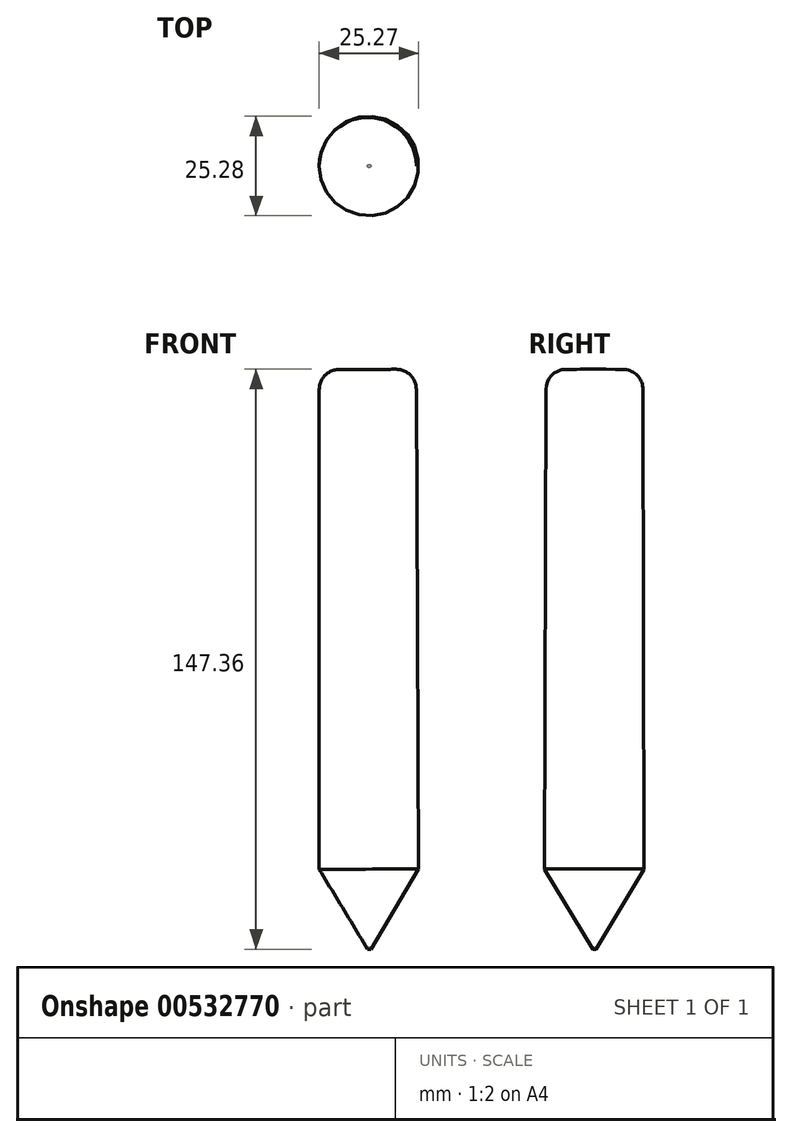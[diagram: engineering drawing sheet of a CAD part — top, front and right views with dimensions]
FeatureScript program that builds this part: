
annotation { "Feature Type Name" : "Feature", "Feature Type Description" : "" }
export const myFeature = defineFeature(function(context is Context, id is Id, definition is map)
    precondition{}
    {
        {
            var Q0;
            Q0=qCreatedBy(makeId("Front.planeOp"),FACE);
            var sketch = newSketch(context, id + "F0", { "sketchPlane" : qUnion([Q0])});
            skLineSegment(sketch, "E0", {"start": v(-60.12, 72.11) * mm, "end": v(-60.12, -54.89) * mm});
            skLineSegment(sketch, "E1", {"start": v(-60.12, 72.11) * mm, "end": v(-34.72, 72.11) * mm});
            skLineSegment(sketch, "E2", {"start": v(-34.72, 72.11) * mm, "end": v(-34.72, -54.89) * mm});
            skLineSegment(sketch, "E3", {"start": v(-60.12, -54.89) * mm, "end": v(-34.72, -54.89) * mm});
            skLineSegment(sketch, "E4", {"start": v(-60.12, -54.89) * mm, "end": v(-47.85, -75.2) * mm});
            skLineSegment(sketch, "E5", {"start": v(-34.72, -54.89) * mm, "end": v(-47.85, -75.2) * mm});
            skLineSegment(sketch, "E6", {"start": v(-60.12, 46.71) * mm, "end": v(-34.72, 46.71) * mm});
            skLineSegment(sketch, "E7", {"start": v(-47.42, -80.28) * mm, "end": v(-47.85, 86.18) * mm});
            skPoint(sketch, "E7.startSnap0", {"position": v(-47.42, 46.71) * mm});
            skSolve(sketch);
        }
        {
            var Q0;
            {var subQ0=sQuery(id+"F0.wireOp",EDGE,"E1");var subQ1=sQuery(id+"F0.wireOp",EDGE,"E0");var subQ2=makeQuery(id+"F0.imprint","INTERSECT",VERTEX,{"derivedFrom":[subQ1,subQ0]});Q0=makeQuery(id+"F0.imprint","IMPRINT",FACE,{"disambiguationData":[TD([[makeQuery(id+"F0.imprint","IMPRINT",EDGE,{"disambiguationData":[TD([[subQ2,-1.0]])],"derivedFrom":subQ1}),1.0]])]});}
            var Q1;
            {var subQ1=sQuery(id+"F0.wireOp",EDGE,"E0");var subQ3=sQuery(id+"F0.wireOp",EDGE,"E6");var subQ4=makeQuery(id+"F0.imprint","INTERSECT",VERTEX,{"derivedFrom":[subQ1,subQ3]});Q1=makeQuery(id+"F0.imprint","IMPRINT",FACE,{"disambiguationData":[TD([[makeQuery(id+"F0.imprint","IMPRINT",EDGE,{"disambiguationData":[TD([[subQ4,-1.0]])],"derivedFrom":subQ3}),-1.0]])]});}
            var Q2;
            {var subQ0=sQuery(id+"F0.wireOp",EDGE,"E4");Q2=makeQuery(id+"F0.imprint","IMPRINT",FACE,{"disambiguationData":[TD([[makeQuery(id+"F0.imprint","IMPRINT",EDGE,{"derivedFrom":subQ0}),1.0]])]});}
            var Q3;
            Q3=sQuery(id+"F0.wireOp",EDGE,"E7");
            revolve(context, id + "F1", {"entities" : qUnion([Q0, Q1, Q2]), "axis" : qUnion([Q3]), "revolveType" : RevolveType.FULL});
        }
        {
            var Q0;
            Q0=makeQuery(id+"F1.opRevolve","SWEPT_EDGE",EDGE,{"disambiguationData":[OSD([sQuery(id+"F0.wireOp",EDGE,"E0"),sQuery(id+"F0.wireOp",EDGE,"E1")])]});
            fillet(context, id + "F2", {"entities" : qUnion([Q0]), "radius" : 5.08 * mm, "tangentPropagation" : true, "allowEdgeOverflow" : false});
        }
    });
